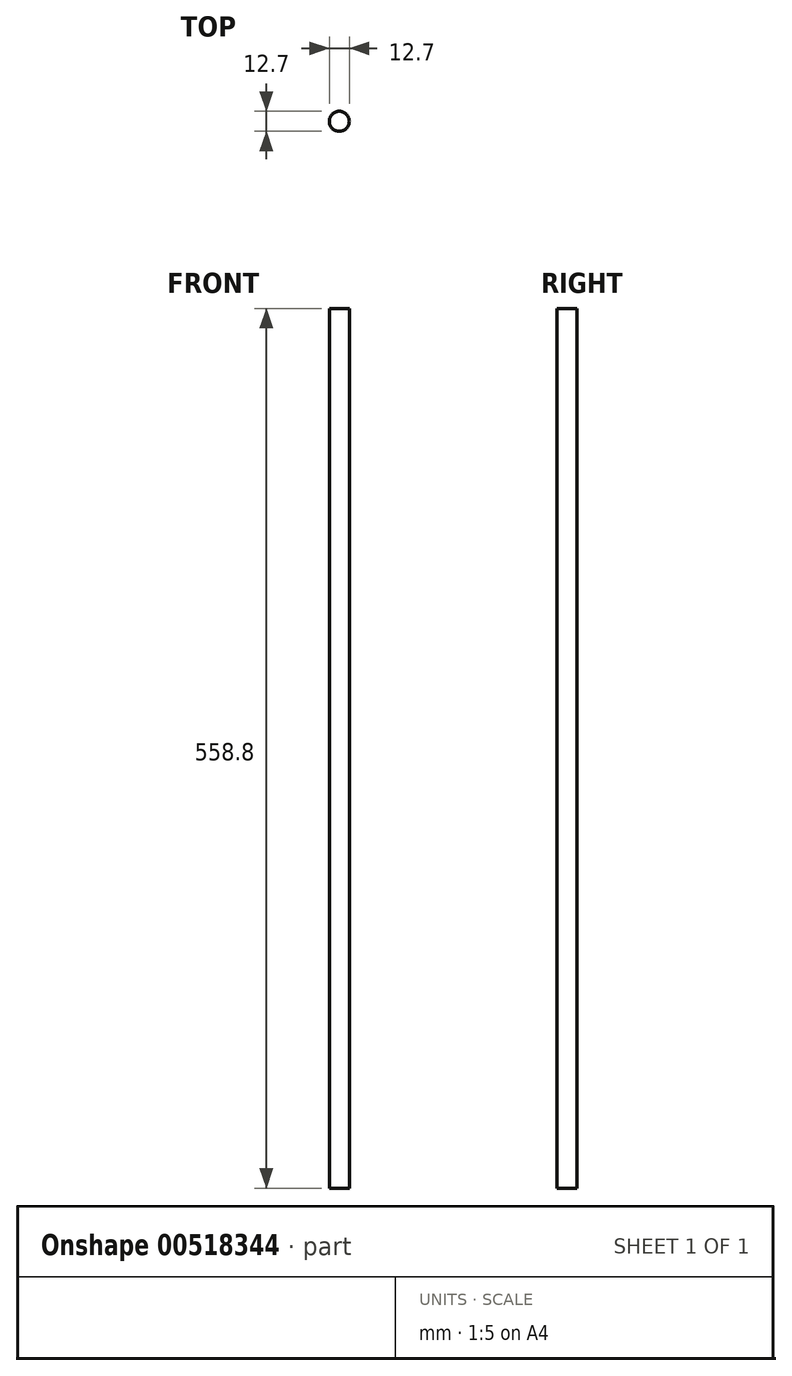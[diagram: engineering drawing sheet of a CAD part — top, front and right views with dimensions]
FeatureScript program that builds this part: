
annotation { "Feature Type Name" : "Feature", "Feature Type Description" : "" }
export const myFeature = defineFeature(function(context is Context, id is Id, definition is map)
    precondition{}
    {
        {
            var Q0;
            Q0=qCreatedBy(makeId("Top.planeOp"),FACE);
            var sketch = newSketch(context, id + "F0", { "sketchPlane" : qUnion([Q0])});
            skCircle(sketch, "E0", {"center": v(0, 0) * mm, "radius": 6.35 * mm});
            skLineSegment(sketch, "E1", {"start": v(0, 0) * mm, "end": v(-4.84, 4.1) * mm});
            skSolve(sketch);
        }
        {
            var Q0;
            Q0=makeQuery(id+"F0.imprint","IMPRINT",FACE,{"disambiguationData":[TD([[makeQuery(id+"F0.imprint","IMPRINT",EDGE,{"derivedFrom":sQuery(id+"F0.wireOp",EDGE,"E0")}),1.0]])]});
            extrude(context, id + "F1", {"entities" : qUnion([Q0]), "depth" : 558.8 * mm, "offsetDistance" : 25.4 * mm});
        }
    });
